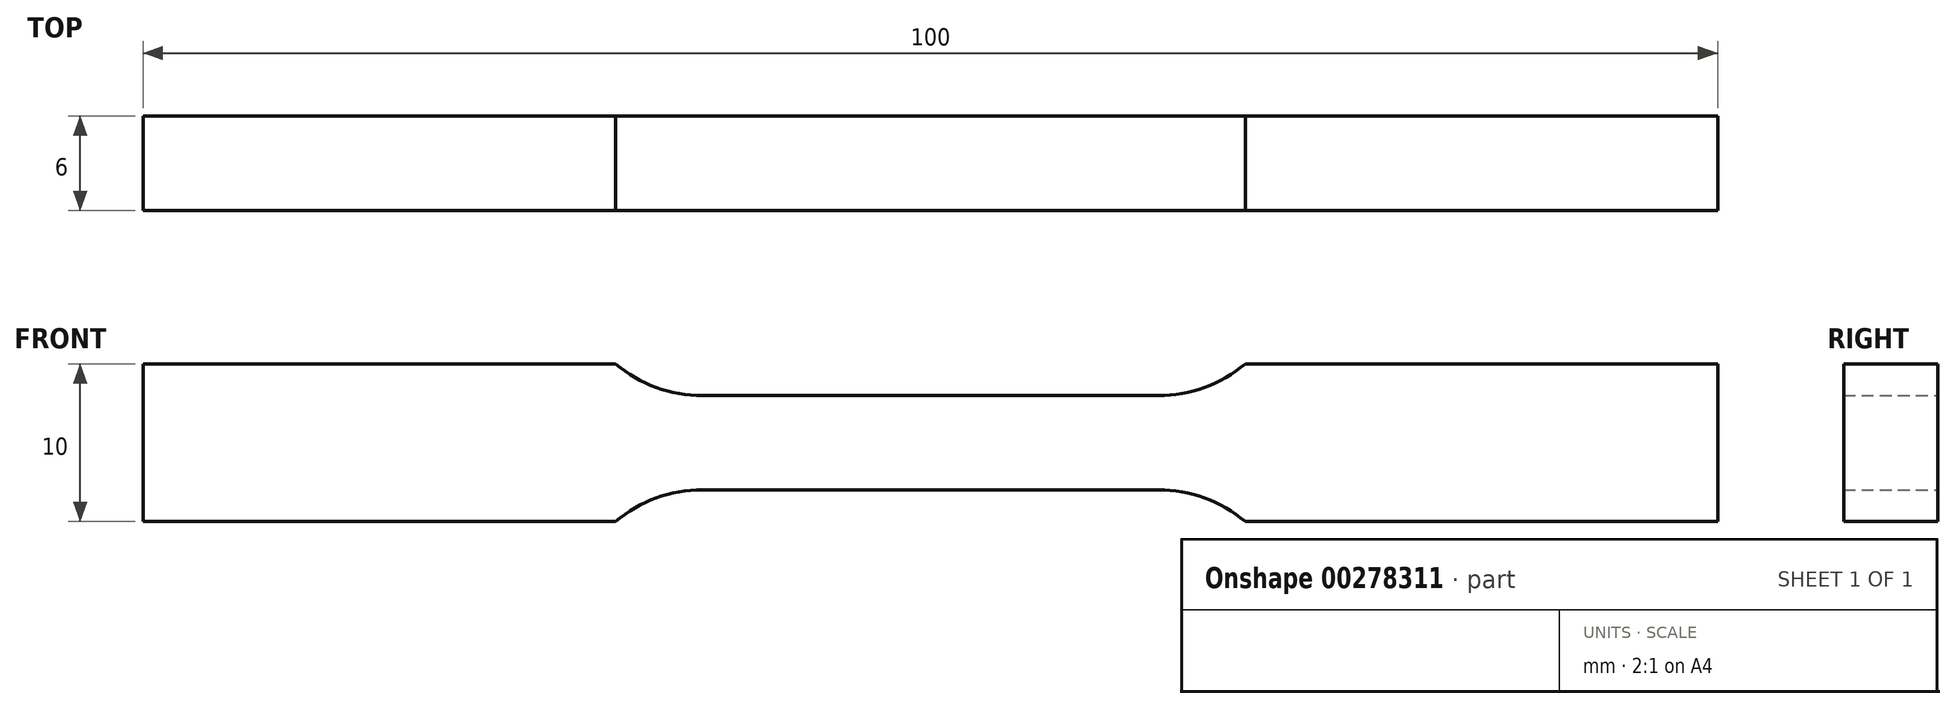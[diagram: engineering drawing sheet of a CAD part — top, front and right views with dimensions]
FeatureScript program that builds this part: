
annotation { "Feature Type Name" : "Feature", "Feature Type Description" : "" }
export const myFeature = defineFeature(function(context is Context, id is Id, definition is map)
    precondition{}
    {
        {
            var Q0;
            Q0=qCreatedBy(makeId("Front.planeOp"),FACE);
            var sketch = newSketch(context, id + "F0", { "sketchPlane" : qUnion([Q0])});
            skLineSegment(sketch, "E0", {"start": v(0, 3) * mm, "end": v(14.48, 3) * mm});
            skArc(sketch, "E1", {"start": v(14.48, 3) * mm, "mid": v(17.41, 3.52) * mm, "end": v(20, 5) * mm});
            skLineSegment(sketch, "E2", {"start": v(20, 5) * mm, "end": v(50, 5) * mm});
            skLineSegment(sketch, "E3", {"start": v(50, 5) * mm, "end": v(50, 0) * mm});
            skLineSegment(sketch, "E4.MirrorCS", {"start": v(0, -3) * mm, "end": v(14.48, -3) * mm});
            skLineSegment(sketch, "E5.MirrorCS", {"start": v(50, -5) * mm, "end": v(50, 0) * mm});
            skLineSegment(sketch, "E6.MirrorCS", {"start": v(20, -5) * mm, "end": v(50, -5) * mm});
            skArc(sketch, "E7.MirrorCS", {"start": v(14.48, -3) * mm, "mid": v(17.41, -3.52) * mm, "end": v(20, -5) * mm});
            skArc(sketch, "E8.MirrorCS", {"start": v(-14.48, -3) * mm, "mid": v(-17.41, -3.52) * mm, "end": v(-20, -5) * mm});
            skLineSegment(sketch, "E9.MirrorCS", {"start": v(-20, -5) * mm, "end": v(-50, -5) * mm});
            skArc(sketch, "E10.MirrorCS", {"start": v(-14.48, 3) * mm, "mid": v(-17.41, 3.52) * mm, "end": v(-20, 5) * mm});
            skLineSegment(sketch, "E11.MirrorCS", {"start": v(-20, 5) * mm, "end": v(-50, 5) * mm});
            skLineSegment(sketch, "E12.MirrorCS", {"start": v(-50, -5) * mm, "end": v(-50, 0) * mm});
            skLineSegment(sketch, "E13.MirrorCS", {"start": v(0, -3) * mm, "end": v(-14.48, -3) * mm});
            skLineSegment(sketch, "E14.MirrorCS", {"start": v(-50, 5) * mm, "end": v(-50, 0) * mm});
            skLineSegment(sketch, "E15.MirrorCS", {"start": v(0, 3) * mm, "end": v(-14.48, 3) * mm});
            skSolve(sketch);
        }
        {
            var Q0;
            Q0 = qSketchRegion(id + "F0", true);
            extrude(context, id + "F1", {"entities" : qUnion([Q0]), "endBound" : BoundingType.SYMMETRIC, "depth" : 6 * mm});
        }
    });
